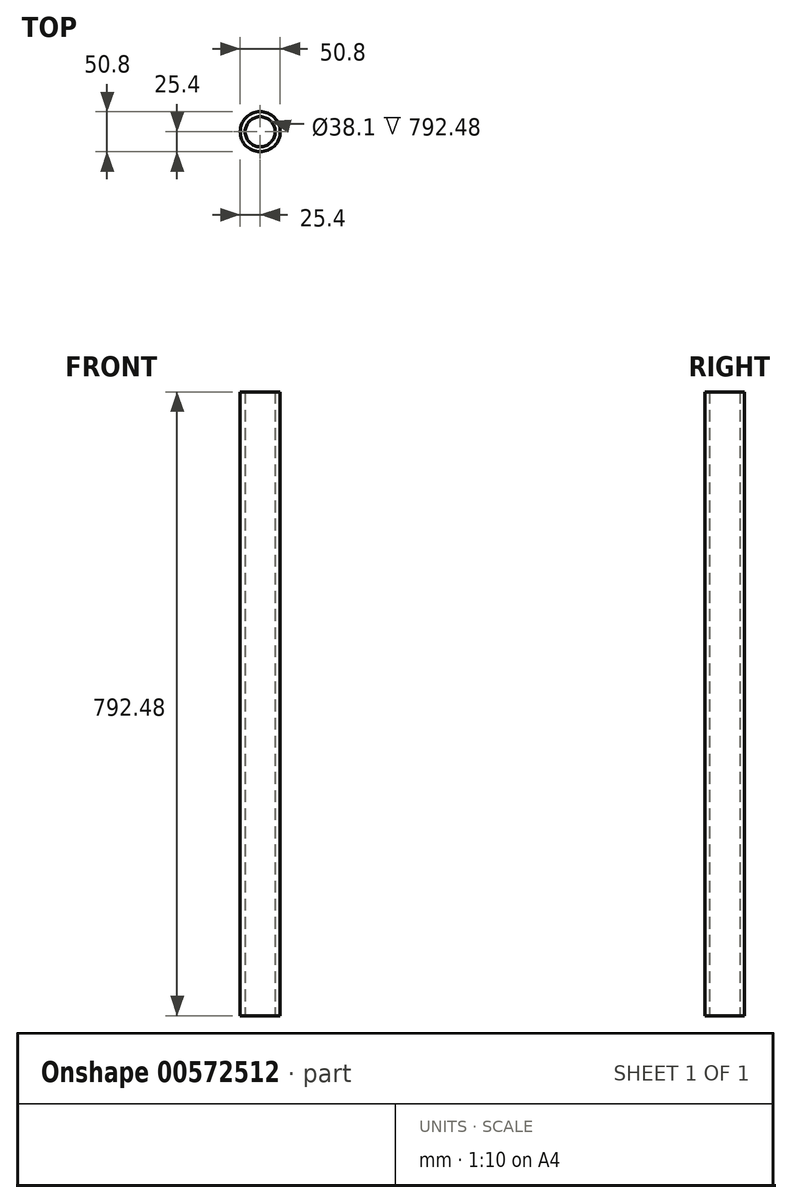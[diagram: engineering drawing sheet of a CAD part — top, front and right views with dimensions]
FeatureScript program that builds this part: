
annotation { "Feature Type Name" : "Feature", "Feature Type Description" : "" }
export const myFeature = defineFeature(function(context is Context, id is Id, definition is map)
    precondition{}
    {
        {
            var Q0;
            Q0=qCreatedBy(makeId("Top.planeOp"),FACE);
            var sketch = newSketch(context, id + "F0", { "sketchPlane" : qUnion([Q0])});
            skCircle(sketch, "E0", {"center": v(0, 0) * mm, "radius": 25.4 * mm});
            skCircle(sketch, "E1", {"center": v(0, 0) * mm, "radius": 19.05 * mm});
            skSolve(sketch);
        }
        {
            var Q0;
            Q0 = qSketchRegion(id + "F0", true);
            extrude(context, id + "F1", {"entities" : qUnion([Q0]), "depth" : 792.48 * mm, "offsetDistance" : 25.4 * mm});
        }
    });
